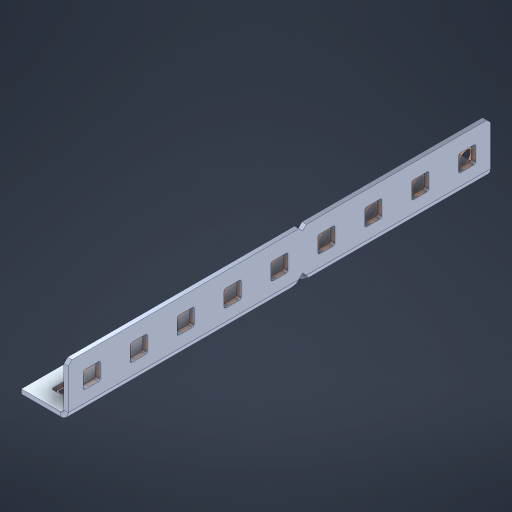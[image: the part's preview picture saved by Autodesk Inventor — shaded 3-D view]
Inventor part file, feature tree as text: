
AUTODESK INVENTOR PART (.ipt)
format: ipt  version: 2023 (Build 270158000, 158)  size: 527,872 bytes
history: native  units: in
note: dims shown in document units (in); Inventor stores cm internally (conversion verified against a paired STEP export)
features: other x23, extrude x17, sheet_metal_op x10, sketch x8, mirror x1, pattern_linear x1, chamfer x1
ambient origin geometry x8: Origin, YZ Plane, XZ Plane, XY Plane, X Axis, Y Axis, Z Axis, Center Point
bodies: Solid1 (feature_tree), Body (feature_tree)
feature tree (61):
  other  "Flange Pattern Plane"
  sheet_metal_op  "Flange Pattern"
  sheet_metal_op  "Body Pattern"
  other  "Arc Length"
  mirror  "Notch Mirror"
  pattern_linear  "Notch Pattern"  Spacing1=0.1875in  [1 undecoded]
  chamfer  "End Chamfer"
  extrude  "Half Cut"  Depth=0.0469in
  sketch  "Sketch1"  dims[d0=2.5in]
  other  "Plate1"
  sketch  "Sketch2"  dims[d1=4.5in]
  other  "Plate2"
  sheet_metal_op  "Bend1"
  sheet_metal_op  "Corner1"
  sketch  "Sketch3"  dims[d2=0.0469in]
  other  "Flange Pattern Sketch"
  sketch  "Sketch7"  dims[d3=0.0469in]
  other  "Srf1"
  other  "Srf2"
  sketch  "Sketch8"  dims[d4=0.0234in]
  sketch  "Sketch9"  dims[d5=0.0938in]
  other  "Srf91"
  sheet_metal_op  "Body Pattern Sketch"
  other  "Srf92"
  sketch  "Sketch13"  dims[d6=0.0469in]
  sketch  "Sketch14"  dims[d7=0.5in d8=90.0deg d9=0.0312in d10=0.1875in d11=0.0469in d12=0.0469in d16=0.182in d17=0.02in d18=0.0469in d19=0.0in d20=0.25in d21=0.25in d46=0.172in d47=1.0in d48=0.0in d49=0.182in d50=0.02in d51=0.25in d52=0.25in d53=0.0469in d54=0.0in d55=0.172in d56=1.0in d57=0.0in d60=3.5433in d62=0.5in d63=0.3937in d65=0.5in d85=0.1227in d86=0.1659in d88=0.04in d89=0.0469in d90=0.0in d91=0.04in d92=0.0491in d95=2.5in d96=0.04in d97=0.25in d98=45.0deg d101=0.0in d102=2.497in d131=0.5in d132=3.5433in d134=0.5in d139=0.5in]
  other  "Srf856"
  other  "Srf1310"
  other  "Srf1311"
  other  "Srf1312"
  other  "Srf1376"
  other  "Srf1377"
  other  "Srf1728"
  other  "Srf1755"
  other  "Srf1878"
  other  "Srf1879"
  other  "Srf1880"
  other  "Srf1942"
  other  "Srf1943"
  other  "Srf1944"
  sheet_metal_op  "Flange Stamp"
  sheet_metal_op  "Flange Circle"
  sheet_metal_op  "Body Stamp"
  sheet_metal_op  "Body Circle"
  sheet_metal_op  "Notch"
  extrude  "ExtrusionSrf2"  Depth=0.0469in
  extrude  "ExtrusionSrf92"  Depth=0.5in
  extrude  "ExtrusionSrf856"  Depth=0.02in
  extrude  "ExtrusionSrf1310"  Depth=0.0469in
  extrude  "ExtrusionSrf1311"  TaperAngle=0.0deg  [1 undecoded]
  extrude  "ExtrusionSrf1312"  Depth=0.5in
  extrude  "ExtrusionSrf1376"  Depth=0.5in
  extrude  "ExtrusionSrf1377"  Depth=0.5in
  extrude  "ExtrusionSrf1728"  Depth=0.5in TaperAngle=0.0deg
  extrude  "ExtrusionSrf1755"  Depth=0.5in
  extrude  "ExtrusionSrf1878"  Depth=0.02in
  extrude  "ExtrusionSrf1879"  Depth=0.5in
  extrude  "ExtrusionSrf1880"  Depth=0.5in
  extrude  "ExtrusionSrf1942"  Depth=0.0469in
  extrude  "ExtrusionSrf1943"  TaperAngle=0.0deg  [1 undecoded]
  extrude  "ExtrusionSrf1944"  Depth=0.5in
note: 3 required parameter values undecoded (feature->parameter linkage not recoverable at this tier; creation-order binding heuristic only, values carry confidence <= 0.55)
